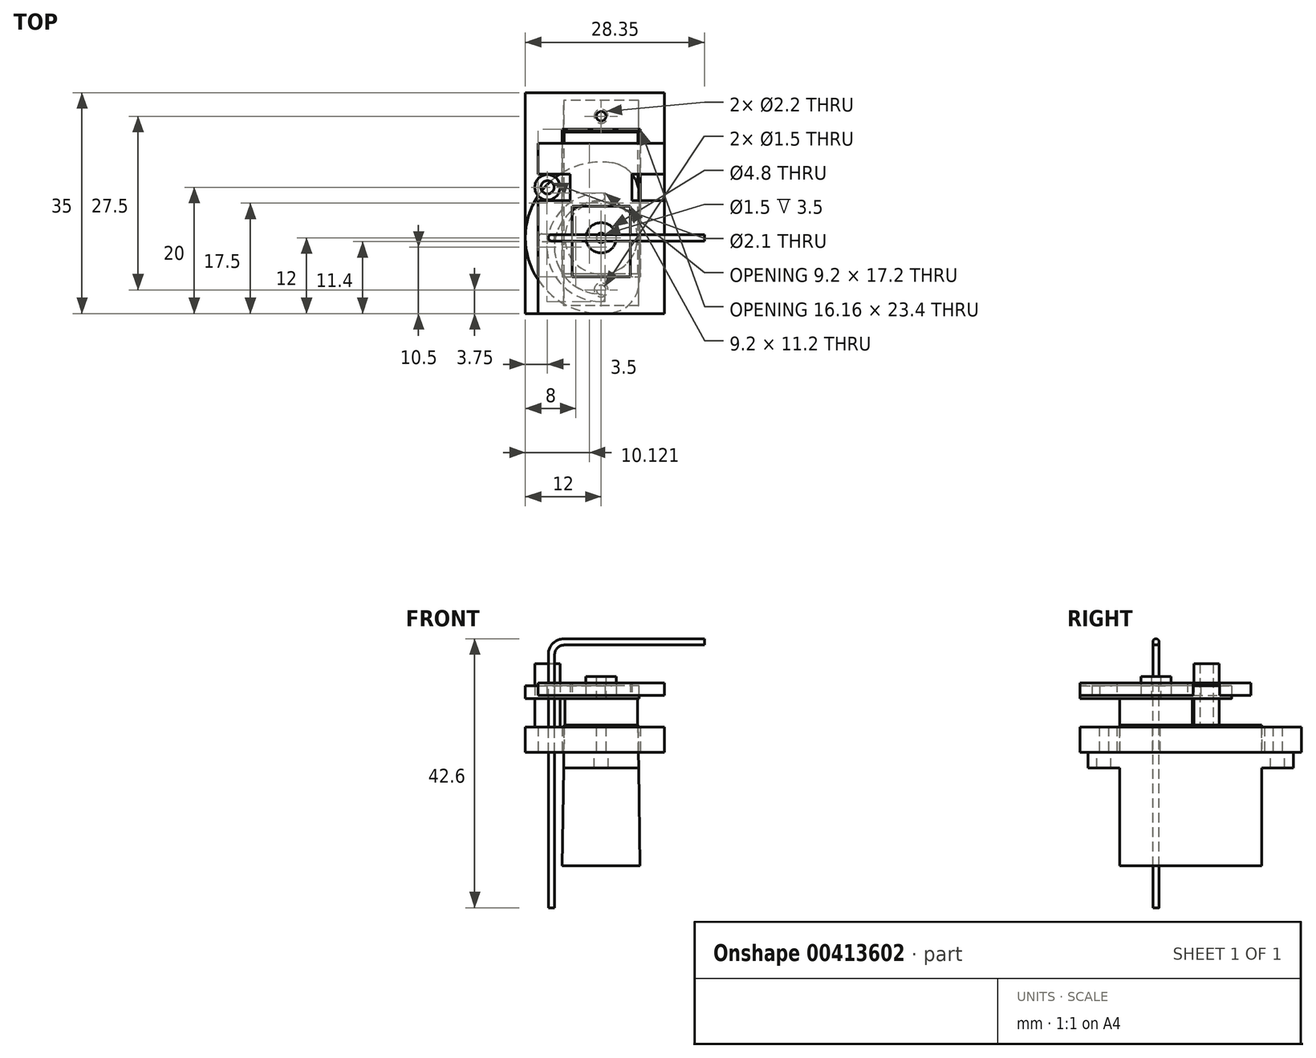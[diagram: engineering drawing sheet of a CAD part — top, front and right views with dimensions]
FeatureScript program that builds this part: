
annotation { "Feature Type Name" : "Feature", "Feature Type Description" : "" }
export const myFeature = defineFeature(function(context is Context, id is Id, definition is map)
    precondition{}
    {
        {
            var Q0;
            Q0=qCreatedBy(makeId("Top.planeOp"),FACE);
            var sketch = newSketch(context, id + "F0", { "sketchPlane" : qUnion([Q0])});
            skCircle(sketch, "E0", {"center": v(0, 0) * mm, "radius": 1.5 * mm});
            skCircle(sketch, "E1", {"center": v(0, -8.25) * mm, "radius": 1 * mm});
            skCircle(sketch, "E2", {"center": v(0, 19.25) * mm, "radius": 1 * mm});
            skLineSegment(sketch, "E3.bottom", {"start": v(-6, 17) * mm, "end": v(6, 17) * mm});
            skLineSegment(sketch, "E3.top", {"start": v(-6, -6) * mm, "end": v(6, -6) * mm});
            skLineSegment(sketch, "E3.left", {"start": v(-6, 17) * mm, "end": v(-6, -6) * mm});
            skLineSegment(sketch, "E3.right", {"start": v(6, 17) * mm, "end": v(6, -6) * mm});
            skPoint(sketch, "E4", {"position": v(0, 17) * mm});
            skPoint(sketch, "E5", {"position": v(6, 5.5) * mm});
            skLineSegment(sketch, "E6", {"start": v(0, 19.25) * mm, "end": v(0, 17) * mm});
            skLineSegment(sketch, "E7", {"start": v(0, -6) * mm, "end": v(0, -8.25) * mm});
            skCircle(sketch, "E8", {"center": v(0, 0) * mm, "radius": 12 * mm});
            skArc(sketch, "E9", {"start": v(0, 6.5) * mm, "mid": v(-8, -1.5) * mm, "end": v(0, -9.5) * mm});
            skCircle(sketch, "E10", {"center": v(-7.86, 0) * mm, "radius": 0.6 * mm});
            skSolve(sketch);
        }
        {
            var Q0;
            Q0=qCreatedBy(makeId("Front.planeOp"),FACE);
            var sketch = newSketch(context, id + "F1", { "sketchPlane" : qUnion([Q0])});
            skLineSegment(sketch, "E11", {"start": v(16.35, 17.47) * mm, "end": v(-5.86, 17.47) * mm});
            skLineSegment(sketch, "E12", {"start": v(-7.86, 15.47) * mm, "end": v(-7.86, -24.63) * mm});
            skPoint(sketch, "E13.visualSharp", {"position": v(-7.86, 17.47) * mm});
            skArc(sketch, "E13.filletArc", {"start": v(-5.86, 17.47) * mm, "mid": v(-7.27, 16.88) * mm, "end": v(-7.86, 15.47) * mm});
            skSolve(sketch);
        }
        {
            var Q0;
            Q0=qCreatedBy(makeId("Top.planeOp"),FACE);
            var Q1;
            Q1=sQuery(id+"F1.wireOp",VERTEX,"E12.end");
            cPlane(context, id + "F2", {"entities" : qUnion([Q0, Q1]), "cplaneType" : CPlaneType.PLANE_POINT, "offset" : 25 * mm, "width" : 150 * mm, "height" : 150 * mm});
        }
        {
            var Q0;
            Q0=qCreatedBy(makeId("Right.planeOp"),FACE);
            var sketch = newSketch(context, id + "F3", { "sketchPlane" : qUnion([Q0])});
            skLineSegment(sketch, "E14", {"start": v(-10.75, 0) * mm, "end": v(-10.75, -2.5) * mm});
            skLineSegment(sketch, "E15", {"start": v(-10.75, -2.5) * mm, "end": v(-5.75, -2.5) * mm});
            skLineSegment(sketch, "E16", {"start": v(-5.75, -2.5) * mm, "end": v(-5.75, -18) * mm});
            skLineSegment(sketch, "E17", {"start": v(-5.75, -18) * mm, "end": v(16.75, -18) * mm});
            skLineSegment(sketch, "E18", {"start": v(16.75, -18) * mm, "end": v(16.75, -2.5) * mm});
            skLineSegment(sketch, "E19", {"start": v(16.75, -2.5) * mm, "end": v(21.75, -2.5) * mm});
            skLineSegment(sketch, "E20", {"start": v(21.75, -2.5) * mm, "end": v(21.75, 0) * mm});
            skLineSegment(sketch, "E21", {"start": v(21.75, 0) * mm, "end": v(16.75, 0) * mm});
            skLineSegment(sketch, "E22", {"start": v(16.75, 0) * mm, "end": v(16.75, 4.3) * mm});
            skLineSegment(sketch, "E23", {"start": v(16.75, 4.3) * mm, "end": v(-5.75, 4.3) * mm});
            skLineSegment(sketch, "E24", {"start": v(-5.75, 4.3) * mm, "end": v(-5.75, 0) * mm});
            skLineSegment(sketch, "E25", {"start": v(-5.75, 0) * mm, "end": v(-10.75, 0) * mm});
            skSolve(sketch);
        }
        {
            var Q0;
            Q0=makeQuery(id+"F3.imprint","IMPRINT",FACE,{"disambiguationData":[TD([[makeQuery(id+"F3.imprint","IMPRINT",EDGE,{"derivedFrom":sQuery(id+"F3.wireOp",EDGE,"E14")}),1.0]])]});
            extrude(context, id + "F4", {"entities" : qUnion([Q0]), "endBound" : BoundingType.SYMMETRIC, "depth" : 15 * mm});
        }
        {
            var Q0;
            Q0=qCreatedBy(makeId("Top.planeOp"),FACE);
            var sketch = newSketch(context, id + "F5", { "sketchPlane" : qUnion([Q0])});
            skCircle(sketch, "E26", {"center": v(0, -8.25) * mm, "radius": 1.1 * mm});
            skCircle(sketch, "E27", {"center": v(0, 19.25) * mm, "radius": 1.1 * mm});
            skSolve(sketch);
        }
        {
            var Q0;
            Q0=makeQuery(id+"F5.imprint","IMPRINT",FACE,{"disambiguationData":[TD([[makeQuery(id+"F5.imprint","IMPRINT",EDGE,{"derivedFrom":sQuery(id+"F5.wireOp",EDGE,"E26")}),1.0]])]});
            var Q1;
            Q1=makeQuery(id+"F5.imprint","IMPRINT",FACE,{"disambiguationData":[TD([[makeQuery(id+"F5.imprint","IMPRINT",EDGE,{"derivedFrom":sQuery(id+"F5.wireOp",EDGE,"E27")}),1.0]])]});
            extrude(context, id + "F6", {"entities" : qUnion([Q0, Q1]), "operationType" : NewBodyOperationType.REMOVE, "endBound" : BoundingType.THROUGH_ALL, "oppositeDirection" : true, "depth" : 25 * mm});
        }
        {
            var Q0;
            Q0=makeQuery(id+"F4.opExtrude","SWEPT_FACE",FACE,{"disambiguationData":[OSD([sQuery(id+"F3.wireOp",EDGE,"E23")])]});
            var sketch = newSketch(context, id + "F7", { "sketchPlane" : qUnion([Q0])});
            skCircle(sketch, "E28", {"center": v(0, 0) * mm, "radius": 5.75 * mm});
            skSolve(sketch);
        }
        {
            var Q0;
            Q0=makeQuery(id+"F7.imprint","IMPRINT",FACE,{"disambiguationData":[TD([[makeQuery(id+"F7.imprint","IMPRINT",EDGE,{"derivedFrom":sQuery(id+"F7.wireOp",EDGE,"E28")}),1.0]])]});
            extrude(context, id + "F8", {"entities" : qUnion([Q0]), "operationType" : NewBodyOperationType.ADD, "depth" : 4.2 * mm});
        }
        {
            var Q0;
            Q0=makeQuery(id+"F8.opExtrude","CAP_FACE",FACE,{"disambiguationData":[OSD([sQuery(id+"F7.wireOp",EDGE,"E28")])],"isStart":false});
            var sketch = newSketch(context, id + "F9", { "sketchPlane" : qUnion([Q0])});
            skCircle(sketch, "E29", {"center": v(0, 0) * mm, "radius": 2.4 * mm});
            skCircle(sketch, "E30", {"center": v(0, 0) * mm, "radius": 0.75 * mm});
            skSolve(sketch);
        }
        {
            var Q0;
            Q0=makeQuery(id+"F9.imprint","IMPRINT",FACE,{"disambiguationData":[TD([[makeQuery(id+"F9.imprint","IMPRINT",EDGE,{"derivedFrom":sQuery(id+"F9.wireOp",EDGE,"E29")}),1.0]])]});
            extrude(context, id + "F10", {"entities" : qUnion([Q0]), "operationType" : NewBodyOperationType.ADD, "depth" : 3.5 * mm});
        }
        {
            var Q0;
            Q0=qCreatedBy(makeId("Front.planeOp"),FACE);
            var sketch = newSketch(context, id + "F11", { "sketchPlane" : qUnion([Q0])});
            skLineSegment(sketch, "E31", {"start": v(-6.15, -18) * mm, "end": v(-5.85, 4.3) * mm});
            skLineSegment(sketch, "E32", {"start": v(-5.85, 4.3) * mm, "end": v(-5.85, 12) * mm});
            skLineSegment(sketch, "E33", {"start": v(-5.85, 12) * mm, "end": v(5.85, 12) * mm});
            skLineSegment(sketch, "E34", {"start": v(5.85, 12) * mm, "end": v(5.85, 4.3) * mm});
            skLineSegment(sketch, "E35", {"start": v(5.85, 4.3) * mm, "end": v(6.15, -18) * mm});
            skLineSegment(sketch, "E36", {"start": v(-6.15, -18) * mm, "end": v(6.15, -18) * mm, "construction": true});
            skLineSegment(sketch, "E37", {"start": v(-5.85, 4.3) * mm, "end": v(5.85, 4.3) * mm, "construction": true});
            skPoint(sketch, "E38", {"position": v(0, 12) * mm});
            skPoint(sketch, "E39", {"position": v(0, -18) * mm});
            skLineSegment(sketch, "E40", {"start": v(-6.15, -18) * mm, "end": v(-10.82, -18) * mm});
            skLineSegment(sketch, "E41", {"start": v(-10.82, -18) * mm, "end": v(-10.82, 17.85) * mm});
            skLineSegment(sketch, "E42", {"start": v(-10.82, 17.85) * mm, "end": v(12.06, 17.85) * mm});
            skLineSegment(sketch, "E43", {"start": v(12.06, 17.85) * mm, "end": v(12.06, -18) * mm});
            skLineSegment(sketch, "E44", {"start": v(12.06, -18) * mm, "end": v(6.15, -18) * mm});
            skSolve(sketch);
        }
        {
            var Q0;
            Q0 = qSketchRegion(id + "F11", true);
            extrude(context, id + "F12", {"entities" : qUnion([Q0]), "operationType" : NewBodyOperationType.REMOVE, "endBound" : BoundingType.THROUGH_ALL, "depth" : 25 * mm, "hasSecondDirection" : true, "secondDirectionBound" : SecondDirectionBoundingType.THROUGH_ALL, "secondDirectionOppositeDirection" : true, "secondDirectionDepth" : 25 * mm});
        }
        {
            var Q0;
            Q0=makeQuery(id+"F9.imprint","IMPRINT",FACE,{"disambiguationData":[TD([[makeQuery(id+"F9.imprint","IMPRINT",EDGE,{"derivedFrom":sQuery(id+"F9.wireOp",EDGE,"E29")}),-1.0]])]});
            var sketch = newSketch(context, id + "F13", { "sketchPlane" : qUnion([Q0])});
            skCircle(sketch, "E45.0", {"center": v(0, 0) * mm, "radius": 2.4 * mm});
            skArc(sketch, "E46.JFp.JFp", {"start": v(0, 6.5) * mm, "mid": v(-8, -1.5) * mm, "end": v(0, -9.5) * mm, "construction": true});
            skArc(sketch, "E46.0.startCap", {"start": v(0, 7.1) * mm, "mid": v(0.6, 6.5) * mm, "end": v(0, 5.9) * mm});
            skArc(sketch, "E46.0.endCap", {"start": v(0, -8.9) * mm, "mid": v(0.6, -9.5) * mm, "end": v(0, -10.1) * mm});
            skArc(sketch, "E46.0.left", {"start": v(0, 5.9) * mm, "mid": v(-7.4, -1.5) * mm, "end": v(0, -8.9) * mm});
            skArc(sketch, "E46.0.right", {"start": v(0, 7.1) * mm, "mid": v(-8.6, -1.5) * mm, "end": v(0, -10.1) * mm});
            skArc(sketch, "E47.0", {"start": v(6, 10.4) * mm, "mid": v(-12, 0) * mm, "end": v(6, -10.4) * mm});
            skLineSegment(sketch, "E48", {"start": v(6, 10.4) * mm, "end": v(6, -10.4) * mm});
            skSolve(sketch);
        }
        {
            var Q0;
            Q0 = qSketchRegion(id + "F13", true);
            extrude(context, id + "F14", {"entities" : qUnion([Q0]), "depth" : 2 * mm});
        }
        {
            var Q0;
            Q0=qCreatedBy(makeId("Top.planeOp"),FACE);
            cPlane(context, id + "F15", {"entities" : qUnion([Q0]), "cplaneType" : CPlaneType.OFFSET, "offset" : 9 * mm, "width" : 150 * mm, "height" : 150 * mm});
        }
        {
            var Q0;
            Q0=qCreatedBy(id+"F15.planeOp",FACE);
            var sketch = newSketch(context, id + "F16", { "sketchPlane" : qUnion([Q0])});
            skLineSegment(sketch, "E49.bottom", {"start": v(-10, 15) * mm, "end": v(10, 15) * mm});
            skLineSegment(sketch, "E49.top", {"start": v(-10, -12) * mm, "end": v(10, -12) * mm});
            skLineSegment(sketch, "E49.left", {"start": v(-10, 15) * mm, "end": v(-10, 10.1) * mm});
            skLineSegment(sketch, "E49.right", {"start": v(10, 15) * mm, "end": v(10, 10.1) * mm});
            skLineSegment(sketch, "E50.bottom", {"start": v(-4.6, -6.2) * mm, "end": v(4.6, -6.2) * mm});
            skLineSegment(sketch, "E50.top", {"start": v(-4.6, 5) * mm, "end": v(4.6, 5) * mm});
            skLineSegment(sketch, "E50.left", {"start": v(-4.6, -6.2) * mm, "end": v(-4.6, 5) * mm});
            skLineSegment(sketch, "E50.right", {"start": v(4.6, -6.2) * mm, "end": v(4.6, 5) * mm});
            skPoint(sketch, "E51", {"position": v(0, 5) * mm});
            skPoint(sketch, "E52", {"position": v(0, -12) * mm});
            skLineSegment(sketch, "E53", {"start": v(-10, 5.9) * mm, "end": v(-4.9, 5.9) * mm});
            skLineSegment(sketch, "E54", {"start": v(-4.9, 5.9) * mm, "end": v(-4.9, 10.1) * mm});
            skLineSegment(sketch, "E55", {"start": v(-4.9, 10.1) * mm, "end": v(-10, 10.1) * mm});
            skLineSegment(sketch, "E56", {"start": v(10, 10.1) * mm, "end": v(4.9, 10.1) * mm});
            skLineSegment(sketch, "E57", {"start": v(4.9, 10.1) * mm, "end": v(4.9, 5.9) * mm});
            skLineSegment(sketch, "E58", {"start": v(4.9, 5.9) * mm, "end": v(10, 5.9) * mm});
            skLineSegment(sketch, "E59.trimOffspring", {"start": v(-10, 5.9) * mm, "end": v(-10, -12) * mm});
            skLineSegment(sketch, "E60.trimOffspring", {"start": v(10, 5.9) * mm, "end": v(10, -12) * mm});
            skSolve(sketch);
        }
        {
            var Q0;
            Q0=makeQuery(id+"F16.imprint","IMPRINT",FACE,{"disambiguationData":[TD([[makeQuery(id+"F16.imprint","IMPRINT",EDGE,{"derivedFrom":sQuery(id+"F16.wireOp",EDGE,"E49.bottom")}),-1.0]])]});
            extrude(context, id + "F17", {"entities" : qUnion([Q0]), "depth" : 2 * mm});
        }
        {
            var Q0;
            Q0=qCreatedBy(makeId("Top.planeOp"),FACE);
            var sketch = newSketch(context, id + "F18", { "sketchPlane" : qUnion([Q0])});
            skLineSegment(sketch, "E61.bottom", {"start": v(-12, 23) * mm, "end": v(10, 23) * mm});
            skLineSegment(sketch, "E61.top", {"start": v(-12, -12) * mm, "end": v(10, -12) * mm});
            skLineSegment(sketch, "E61.left", {"start": v(-12, 23) * mm, "end": v(-12, -12) * mm});
            skLineSegment(sketch, "E61.right", {"start": v(10, 23) * mm, "end": v(10, -12) * mm});
            skLineSegment(sketch, "E62.bottom", {"start": v(-6.2, 17.2) * mm, "end": v(6.2, 17.2) * mm});
            skLineSegment(sketch, "E62.top", {"start": v(-6.2, -6.2) * mm, "end": v(6.2, -6.2) * mm});
            skLineSegment(sketch, "E62.left", {"start": v(-6.2, 17.2) * mm, "end": v(-6.2, -6.2) * mm});
            skLineSegment(sketch, "E62.right", {"start": v(6.2, 17.2) * mm, "end": v(6.2, -6.2) * mm});
            skPoint(sketch, "E63", {"position": v(0, 17.2) * mm});
            skPoint(sketch, "E64", {"position": v(-12, 5.5) * mm});
            skPoint(sketch, "E65", {"position": v(-6.2, 5.5) * mm});
            skCircle(sketch, "E66", {"center": v(0, -8.25) * mm, "radius": 0.75 * mm});
            skCircle(sketch, "E67", {"center": v(0, 19.25) * mm, "radius": 0.75 * mm});
            skLineSegment(sketch, "E68", {"start": v(-9.36, 0) * mm, "end": v(-6.36, 0) * mm, "construction": true});
            skPoint(sketch, "E69", {"position": v(-7.86, 0) * mm});
            skArc(sketch, "E70.0.startCap", {"start": v(-9.36, -0.6) * mm, "mid": v(-9.96, 0) * mm, "end": v(-9.36, 0.6) * mm});
            skArc(sketch, "E70.0.endCap", {"start": v(-6.36, 0.6) * mm, "mid": v(-5.76, 0) * mm, "end": v(-6.36, -0.6) * mm});
            skLineSegment(sketch, "E70.0.left", {"start": v(-9.36, 0.6) * mm, "end": v(-6.36, 0.6) * mm});
            skLineSegment(sketch, "E70.0.right", {"start": v(-9.36, -0.6) * mm, "end": v(-6.36, -0.6) * mm});
            skSolve(sketch);
        }
        {
            var Q0;
            Q0=makeQuery(id+"F18.imprint","IMPRINT",FACE,{"disambiguationData":[TD([[makeQuery(id+"F18.imprint","IMPRINT",EDGE,{"derivedFrom":sQuery(id+"F18.wireOp",EDGE,"E61.bottom")}),-1.0]])]});
            extrude(context, id + "F19", {"entities" : qUnion([Q0]), "depth" : 4 * mm});
        }
        {
            var Q0;
            Q0=makeQuery(id+"F19.opExtrude","CAP_FACE",FACE,{"disambiguationData":[OSD([sQuery(id+"F18.wireOp",EDGE,"E61.bottom"),sQuery(id+"F18.wireOp",EDGE,"E61.top"),sQuery(id+"F18.wireOp",EDGE,"E61.left"),sQuery(id+"F18.wireOp",EDGE,"E61.right"),sQuery(id+"F18.wireOp",EDGE,"E62.bottom"),sQuery(id+"F18.wireOp",EDGE,"E62.top"),sQuery(id+"F18.wireOp",EDGE,"E62.left"),sQuery(id+"F18.wireOp",EDGE,"E62.right"),sQuery(id+"F18.wireOp",EDGE,"E66"),sQuery(id+"F18.wireOp",EDGE,"E67")])],"isStart":false});
            var sketch = newSketch(context, id + "F20", { "sketchPlane" : qUnion([Q0])});
            skCircle(sketch, "E71", {"center": v(-8.5, 8) * mm, "radius": 2 * mm});
            skCircle(sketch, "E72", {"center": v(-8.5, 8) * mm, "radius": 1.05 * mm});
            skSolve(sketch);
        }
        {
            var Q0;
            Q0=makeQuery(id+"F20.imprint","IMPRINT",FACE,{"disambiguationData":[TD([[makeQuery(id+"F20.imprint","IMPRINT",EDGE,{"derivedFrom":sQuery(id+"F20.wireOp",EDGE,"E71")}),1.0]])]});
            extrude(context, id + "F21", {"entities" : qUnion([Q0]), "depth" : 10 * mm});
        }
        {
            var Q0;
            Q0=qCreatedBy(id+"F2.planeOp",FACE);
            var sketch = newSketch(context, id + "F22", { "sketchPlane" : qUnion([Q0])});
            skCircle(sketch, "E73", {"center": v(-7.86, 0) * mm, "radius": 0.5 * mm});
            skSolve(sketch);
        }
        {
            var Q0;
            Q0 = qSketchRegion(id + "F22", true);
            var Q1;
            Q1=sQuery(id+"F1.wireOp",EDGE,"E12");
            var Q2;
            Q2=sQuery(id+"F1.wireOp",EDGE,"E13.filletArc");
            var Q3;
            Q3=sQuery(id+"F1.wireOp",EDGE,"E11");
            sweep(context, id + "F23", {"profiles" : qUnion([Q0]), "path" : qUnion([Q1, Q2, Q3])});
        }
        {
            var Q0;
            {var subQ0=sQuery(id+"F13.wireOp",EDGE,"E48");var subQ1=sQuery(id+"F13.wireOp",EDGE,"E47.0");Q0=makeQuery(id+"F14.opExtrude","SWEPT_EDGE",EDGE,{"disambiguationData":[OSD([subQ1,subQ0]),TDD([makeQuery(id+"F13.imprint","INTERSECT",VERTEX,{"disambiguationData":[OD(1.0)],"derivedFrom":[subQ1,subQ0]})])]});}
            var Q1;
            {var subQ0=sQuery(id+"F13.wireOp",EDGE,"E48");var subQ1=sQuery(id+"F13.wireOp",EDGE,"E47.0");Q1=makeQuery(id+"F14.opExtrude","SWEPT_EDGE",EDGE,{"disambiguationData":[OSD([subQ1,subQ0]),TDD([makeQuery(id+"F13.imprint","INTERSECT",VERTEX,{"disambiguationData":[OD(0.0)],"derivedFrom":[subQ1,subQ0]})])]});}
            fillet(context, id + "F24", {"entities" : qUnion([Q0, Q1]), "radius" : 5 * mm, "tangentPropagation" : true, "allowEdgeOverflow" : false});
        }
    });
